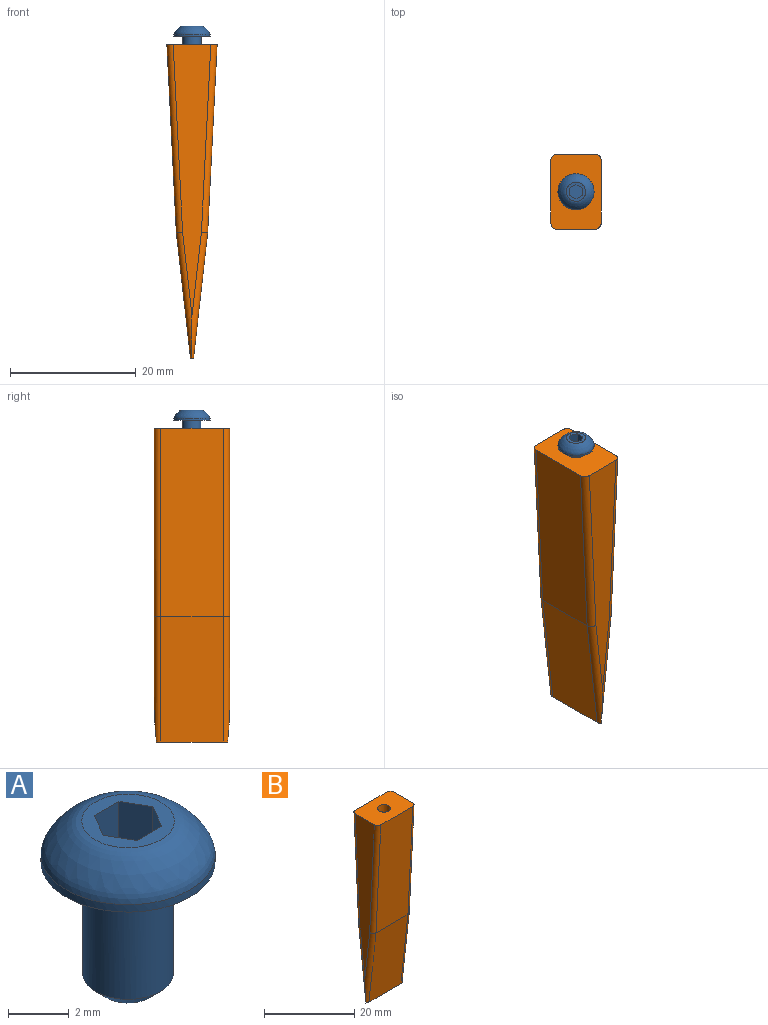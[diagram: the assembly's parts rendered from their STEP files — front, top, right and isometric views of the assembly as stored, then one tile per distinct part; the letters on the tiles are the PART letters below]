
ASSEMBLY  parts=2 mates=1
PART A: 14 faces, bbox 5.8x5.8x6.7 mm
  f0: plane 3.07x3.07mm, normal (0,0,1), area 3.9mm2, adj f3,f4,f5,f6,f7,f8,f10
  f1: cylinder r=2.88mm len=5.75mm, axis (0,0,-1), area 5.4mm2, adj f2,f10
  f2: plane 5.75x5.75mm, normal (0,0,-1), area 18.9mm2, adj f1,f11
  f3: plane 1.5x1mm, normal (-0.87,-0.5,0), area 1.7mm2, adj f0,f4,f8,f9
  f4: plane 1.5x1.15mm, normal (0,-1,0), area 1.7mm2, adj f0,f3,f5,f9
  f5: plane 1.5x1mm, normal (0.87,-0.5,0), area 1.7mm2, adj f0,f4,f6,f9
  f6: plane 1.5x1mm, normal (0.87,0.5,0), area 1.7mm2, adj f0,f5,f7,f9
  f7: plane 1.5x1.15mm, normal (0,1,0), area 1.7mm2, adj f0,f6,f8,f9
  f8: plane 1.5x1mm, normal (-0.87,0.5,0), area 1.7mm2, adj f0,f3,f7,f9
  f9: plane 2.31x2mm, normal (0,0,1), area 3.5mm2, adj f3,f4,f5,f6,f7,f8
  f10: bspline ~5.75x5.75mm, area 29.2mm2, adj f0,f1
  f11: cylinder r=1.5mm len=4.5mm, axis (0,0,1), area 42.4mm2, adj f2,f13
  f12: plane 2x2mm, normal (0,0,-1), area 3.1mm2, adj f13
  f13: cone r=1mm half-angle=45deg, axis (0,0,1), area 5.6mm2, adj f11,f12
PART B: 18 faces, bbox 12x8x50.1 mm
  f0: plane 43.28x6mm, normal (1,0,0), area 154.8mm2, adj f3,f14,f15,f16,f17
  f1: plane 43.28x6mm, normal (-1,0,0), area 154.8mm2, adj f3,f10,f11,f12,f13
  f2: plane 11.33x0.51mm, normal (0,0,-1), area 5.5mm2, adj f6,f7,f11,f12,f16,f17
  f3: plane 12x8mm, normal (0,0,1), area 88.5mm2, adj f0,f1,f4,f5,f8,f10,f13,f14
  f4: plane 30.03x10mm, normal (0,1,-0.05), area 300.6mm2, adj f3,f7,f10,f14
  f5: plane 30.03x10mm, normal (0,-1,-0.05), area 300.6mm2, adj f3,f6,f13,f15
  f6: plane 19.98x10mm, normal (0,-0.99,-0.11), area 201mm2, adj f2,f5,f12,f17
  f7: plane 19.98x10mm, normal (0,0.99,-0.11), area 201mm2, adj f2,f4,f11,f16
  f8: cylinder r=1.45mm len=16mm, axis (0,0,1), area 145.8mm2, adj f3,f9
  f9: plane 2.9x2.9mm, normal (0,0,1), area 6.6mm2, adj f8
  f10: cylinder r=1mm len=30.08mm, axis (0,0.05,1), area 47.2mm2, adj f1,f3,f4,f11
  f11: cylinder r=1mm len=20.11mm, axis (0,-0.11,-0.99), area 28.9mm2, adj f1,f2,f7,f10,f12
  f12: cylinder r=1mm len=20.11mm, axis (0,0.11,-0.99), area 28.9mm2, adj f1,f2,f6,f11,f13
  f13: cylinder r=1mm len=30.08mm, axis (0,-0.05,1), area 47.2mm2, adj f1,f3,f5,f12
  f14: cylinder r=1mm len=30.08mm, axis (0,0.05,1), area 47.2mm2, adj f0,f3,f4,f16
  f15: cylinder r=1mm len=30.08mm, axis (0,-0.05,1), area 47.2mm2, adj f0,f3,f5,f17
  f16: cylinder r=1mm len=20.11mm, axis (0,-0.11,-0.99), area 28.9mm2, adj f0,f2,f7,f14,f17
  f17: cylinder r=1mm len=20.11mm, axis (0,0.11,-0.99), area 28.9mm2, adj f0,f2,f6,f15,f16
PLACE A rot(axis=(0,0,1),90deg) t=(-30.1,21.33,4.5)mm
PLACE B rot(axis=(0,0,1),90deg) t=(-30.1,58.83,3.25)mm
MATE fastened B.f8 <-> A.f1  axis (0,0,1) through (-30.1,33.83,3.25)mm
